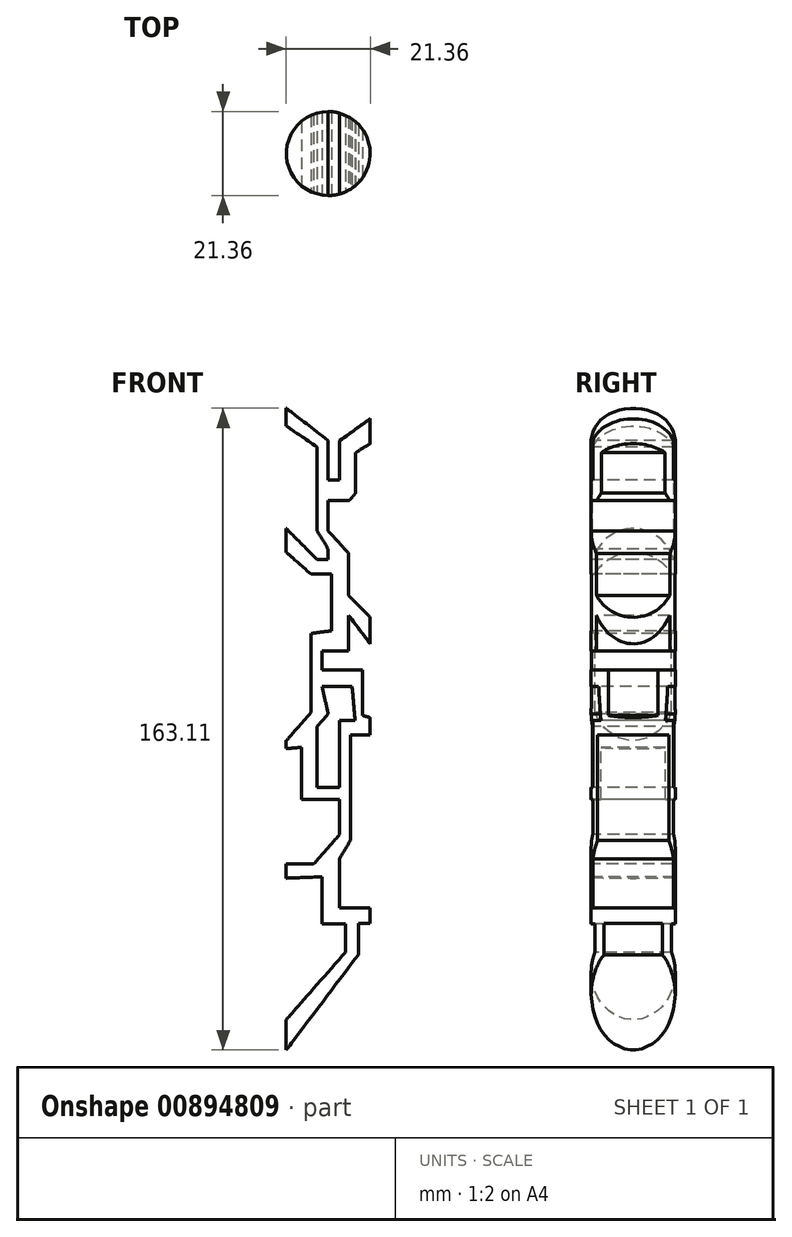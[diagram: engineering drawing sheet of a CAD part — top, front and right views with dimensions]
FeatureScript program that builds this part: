
annotation { "Feature Type Name" : "Feature", "Feature Type Description" : "" }
export const myFeature = defineFeature(function(context is Context, id is Id, definition is map)
    precondition{}
    {
        {
            var Q0;
            Q0=qCreatedBy(makeId("Top.planeOp"),FACE);
            var sketch = newSketch(context, id + "F0", { "sketchPlane" : qUnion([Q0])});
            skCircle(sketch, "E0", {"center": v(0, 0) * mm, "radius": 10.68 * mm});
            skSolve(sketch);
        }
        {
            var Q0;
            Q0=makeQuery(id+"F0.imprint","IMPRINT",FACE,{"disambiguationData":[TD([[makeQuery(id+"F0.imprint","IMPRINT",EDGE,{"derivedFrom":sQuery(id+"F0.wireOp",EDGE,"E0")}),1.0]])]});
            extrude(context, id + "F1", {"entities" : qUnion([Q0]), "oppositeDirection" : true, "depth" : 137.16 * mm, "offsetDistance" : 25.4 * mm});
        }
        {
            var Q0;
            Q0=makeQuery(id+"F1.opExtrude","CAP_FACE",FACE,{"disambiguationData":[OSD([sQuery(id+"F0.wireOp",EDGE,"E0")])],"isStart":true});
            extrude(context, id + "F2", {"entities" : qUnion([Q0]), "operationType" : NewBodyOperationType.ADD, "depth" : 38.1 * mm, "offsetDistance" : 25.4 * mm});
        }
        {
            var Q0;
            Q0=qCreatedBy(makeId("Front.planeOp"),FACE);
            var sketch = newSketch(context, id + "F3", { "sketchPlane" : qUnion([Q0])});
            skLineSegment(sketch, "E1", {"start": v(11.9, 25.61) * mm, "end": v(2.92, 19.17) * mm});
            skLineSegment(sketch, "E2", {"start": v(2.92, 19.17) * mm, "end": v(2.92, 9.17) * mm});
            skLineSegment(sketch, "E3", {"start": v(2.92, 9.17) * mm, "end": v(0, 9.17) * mm});
            skLineSegment(sketch, "E4", {"start": v(0, 9.17) * mm, "end": v(0, 19.17) * mm});
            skLineSegment(sketch, "E5", {"start": v(0, 19.17) * mm, "end": v(-17.06, 32.37) * mm});
            skLineSegment(sketch, "E6", {"start": v(-17.06, 32.37) * mm, "end": v(-15.32, 26.02) * mm});
            skLineSegment(sketch, "E7", {"start": v(-15.32, 26.02) * mm, "end": v(-2.82, 17.56) * mm});
            skLineSegment(sketch, "E8", {"start": v(-2.82, 17.56) * mm, "end": v(-2.82, -3.79) * mm});
            skLineSegment(sketch, "E9", {"start": v(-2.82, -3.79) * mm, "end": v(0, -8.4) * mm});
            skLineSegment(sketch, "E10", {"start": v(0, -8.4) * mm, "end": v(0, -11.1) * mm});
            skLineSegment(sketch, "E11", {"start": v(0, -11.1) * mm, "end": v(-2.82, -11.1) * mm});
            skLineSegment(sketch, "E12", {"start": v(-2.82, -11.1) * mm, "end": v(-13.79, 0) * mm});
            skLineSegment(sketch, "E13", {"start": v(-13.79, 0) * mm, "end": v(-17.06, -8.4) * mm});
            skLineSegment(sketch, "E14", {"start": v(-17.06, -8.4) * mm, "end": v(-13.98, -6.29) * mm});
            skLineSegment(sketch, "E15", {"start": v(-13.98, -6.29) * mm, "end": v(-4.4, -14.73) * mm});
            skLineSegment(sketch, "E16", {"start": v(-4.4, -14.73) * mm, "end": v(0.87, -14.73) * mm});
            skLineSegment(sketch, "E17", {"start": v(0.87, -14.73) * mm, "end": v(0.87, -29.14) * mm});
            skLineSegment(sketch, "E18", {"start": v(0.87, -29.14) * mm, "end": v(-4.4, -29.83) * mm});
            skLineSegment(sketch, "E19", {"start": v(-4.4, -29.83) * mm, "end": v(-4.4, -49.94) * mm});
            skLineSegment(sketch, "E20", {"start": v(-4.4, -49.94) * mm, "end": v(-12.61, -59.27) * mm});
            skLineSegment(sketch, "E21", {"start": v(-12.61, -59.27) * mm, "end": v(-6.85, -58.77) * mm});
            skLineSegment(sketch, "E22", {"start": v(-6.85, -58.77) * mm, "end": v(-6.85, -71.97) * mm});
            skLineSegment(sketch, "E23", {"start": v(-6.85, -71.97) * mm, "end": v(2.92, -71.97) * mm});
            skLineSegment(sketch, "E24", {"start": v(2.92, -71.97) * mm, "end": v(2.92, -80.9) * mm});
            skLineSegment(sketch, "E25", {"start": v(2.92, -80.9) * mm, "end": v(-3.68, -88.4) * mm});
            skLineSegment(sketch, "E26", {"start": v(-3.68, -88.4) * mm, "end": v(-13.98, -88.4) * mm});
            skLineSegment(sketch, "E27", {"start": v(-13.98, -88.4) * mm, "end": v(-13.66, -92.11) * mm});
            skLineSegment(sketch, "E28", {"start": v(-13.66, -92.11) * mm, "end": v(-1.57, -91.66) * mm});
            skLineSegment(sketch, "E29", {"start": v(-1.57, -91.66) * mm, "end": v(-1.57, -103.58) * mm});
            skLineSegment(sketch, "E30", {"start": v(-1.57, -103.58) * mm, "end": v(4.43, -103.58) * mm});
            skLineSegment(sketch, "E31", {"start": v(4.43, -103.58) * mm, "end": v(4.43, -110.8) * mm});
            skLineSegment(sketch, "E32", {"start": v(4.43, -110.8) * mm, "end": v(-17.06, -135.21) * mm});
            skLineSegment(sketch, "E33", {"start": v(-17.06, -135.21) * mm, "end": v(-13.98, -140.04) * mm});
            skLineSegment(sketch, "E34", {"start": v(-13.98, -140.04) * mm, "end": v(7.65, -111.46) * mm});
            skLineSegment(sketch, "E35", {"start": v(7.65, -111.46) * mm, "end": v(7.65, -103.55) * mm});
            skLineSegment(sketch, "E36", {"start": v(7.65, -103.55) * mm, "end": v(17.08, -103.55) * mm});
            skLineSegment(sketch, "E37", {"start": v(17.08, -103.55) * mm, "end": v(16.74, -99.54) * mm});
            skLineSegment(sketch, "E38", {"start": v(16.74, -99.54) * mm, "end": v(2.92, -99.54) * mm});
            skLineSegment(sketch, "E39", {"start": v(2.92, -99.54) * mm, "end": v(2.92, -87.05) * mm});
            skLineSegment(sketch, "E40", {"start": v(2.92, -87.05) * mm, "end": v(5.66, -82.35) * mm});
            skLineSegment(sketch, "E41", {"start": v(5.66, -82.35) * mm, "end": v(5.66, -55.57) * mm});
            skLineSegment(sketch, "E42", {"start": v(5.66, -55.57) * mm, "end": v(13.82, -55.57) * mm});
            skLineSegment(sketch, "E43", {"start": v(13.82, -55.57) * mm, "end": v(13.82, -51.96) * mm});
            skLineSegment(sketch, "E44", {"start": v(13.82, -51.96) * mm, "end": v(8.65, -50.68) * mm});
            skLineSegment(sketch, "E45", {"start": v(8.65, -50.68) * mm, "end": v(8.65, -39.09) * mm});
            skLineSegment(sketch, "E46", {"start": v(8.65, -39.09) * mm, "end": v(-1.57, -39.09) * mm});
            skLineSegment(sketch, "E47", {"start": v(-1.57, -39.09) * mm, "end": v(-1.57, -34.31) * mm});
            skLineSegment(sketch, "E48", {"start": v(-1.57, -34.31) * mm, "end": v(5.18, -34.31) * mm});
            skLineSegment(sketch, "E49", {"start": v(5.18, -34.31) * mm, "end": v(5.18, -25.21) * mm});
            skLineSegment(sketch, "E50", {"start": v(5.18, -25.21) * mm, "end": v(12.16, -34.44) * mm});
            skLineSegment(sketch, "E51", {"start": v(12.16, -34.44) * mm, "end": v(15.51, -30.63) * mm});
            skLineSegment(sketch, "E52", {"start": v(15.51, -30.63) * mm, "end": v(5.2, -20.2) * mm});
            skLineSegment(sketch, "E53", {"start": v(5.2, -20.2) * mm, "end": v(5.2, -9.48) * mm});
            skLineSegment(sketch, "E54", {"start": v(5.2, -9.48) * mm, "end": v(0, -3.79) * mm});
            skLineSegment(sketch, "E55", {"start": v(0, -3.79) * mm, "end": v(0, 3.9) * mm});
            skLineSegment(sketch, "E56", {"start": v(0, 3.9) * mm, "end": v(5.3, 3.9) * mm});
            skLineSegment(sketch, "E57", {"start": v(5.3, 3.9) * mm, "end": v(6.98, 5.82) * mm});
            skLineSegment(sketch, "E58", {"start": v(6.98, 5.82) * mm, "end": v(6.98, 16.13) * mm});
            skLineSegment(sketch, "E59", {"start": v(6.98, 16.13) * mm, "end": v(15.74, 21.56) * mm});
            skLineSegment(sketch, "E60", {"start": v(15.74, 21.56) * mm, "end": v(11.9, 25.61) * mm});
            skLineSegment(sketch, "E61", {"start": v(-1.57, -43.35) * mm, "end": v(6.07, -43.35) * mm});
            skLineSegment(sketch, "E62", {"start": v(6.07, -43.35) * mm, "end": v(6.8, -51.88) * mm});
            skLineSegment(sketch, "E63", {"start": v(6.8, -51.88) * mm, "end": v(2.92, -51.88) * mm});
            skLineSegment(sketch, "E64", {"start": v(2.92, -51.88) * mm, "end": v(2.92, -68.98) * mm});
            skLineSegment(sketch, "E65", {"start": v(2.92, -68.98) * mm, "end": v(-2.82, -68.98) * mm});
            skLineSegment(sketch, "E66", {"start": v(-2.82, -68.98) * mm, "end": v(-2.82, -53.44) * mm});
            skLineSegment(sketch, "E67", {"start": v(-2.82, -53.44) * mm, "end": v(0, -50.24) * mm});
            skLineSegment(sketch, "E68", {"start": v(0, -50.24) * mm, "end": v(-1.57, -43.35) * mm});
            skLineSegment(sketch, "E69.bottom", {"start": v(-36.44, 47.03) * mm, "end": v(37.41, 47.03) * mm});
            skLineSegment(sketch, "E69.top", {"start": v(-36.44, -157.6) * mm, "end": v(37.41, -157.6) * mm});
            skLineSegment(sketch, "E69.left", {"start": v(-36.44, 47.03) * mm, "end": v(-36.44, -157.6) * mm});
            skLineSegment(sketch, "E69.right", {"start": v(37.41, 47.03) * mm, "end": v(37.41, -157.6) * mm});
            skSolve(sketch);
        }
        {
            var Q0;
            Q0=makeQuery(id+"F3.imprint","IMPRINT",FACE,{"disambiguationData":[TD([[makeQuery(id+"F3.imprint","IMPRINT",EDGE,{"derivedFrom":sQuery(id+"F3.wireOp",EDGE,"E1")}),-1.0]])]});
            var Q1;
            Q1=makeQuery(id+"F3.imprint","IMPRINT",FACE,{"disambiguationData":[TD([[makeQuery(id+"F3.imprint","IMPRINT",EDGE,{"derivedFrom":sQuery(id+"F3.wireOp",EDGE,"E61")}),-1.0]])]});
            extrude(context, id + "F4", {"entities" : qUnion([Q0, Q1]), "operationType" : NewBodyOperationType.REMOVE, "oppositeDirection" : true, "depth" : 25.4 * mm, "offsetDistance" : 25.4 * mm, "symmetric" : true});
        }
    });
